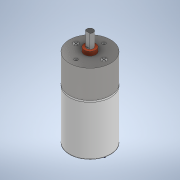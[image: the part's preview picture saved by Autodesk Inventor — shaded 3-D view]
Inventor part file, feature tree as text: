
AUTODESK INVENTOR PART (.ipt)
format: ipt  version: 2022 (Build 260153000, 153)  size: 355,840 bytes
history: native  units: in
note: dims shown in document units (in); Inventor stores cm internally (conversion verified against a paired STEP export)
features: extrude x13, sketch x13, fillet x4, chamfer x1
ambient origin geometry x8: Origin, YZ Plane, XZ Plane, XY Plane, X Axis, Y Axis, Z Axis, Center Point
bodies: Solid1 (feature_tree)
feature tree (31):
  extrude  "Extrusion1"  Depth=1.2205in TaperAngle=0.0deg
  fillet  "Fillet1"  Radius=0.0394in
  extrude  "Extrusion2"  Depth=0.6693in
  extrude  "Extrusion3"  Depth=0.0787in
  extrude  "Extrusion4"  Depth=0.1181in
  extrude  "Extrusion5"  Depth=0.0787in TaperAngle=0.0deg
  fillet  "Fillet2"  Radius=0.1102in
  extrude  "Extrusion6"  Depth=0.0787in TaperAngle=0.0deg
  extrude  "Extrusion7"  Depth=0.0394in
  extrude  "Extrusion8"  Depth=0.0787in
  extrude  "Extrusion9"  Depth=0.0039in
  chamfer  "Chamfer1"  Distance=0.0118in
  extrude  "Extrusion10"  Depth=0.0079in
  extrude  "Extrusion11"  Depth=0.0079in
  extrude  "Extrusion12"  Depth=0.0079in
  fillet  "Fillet3"  Radius=0.0079in
  extrude  "Extrusion13"  Depth=0.7874in
  fillet  "Fillet4"  Radius=0.2756in
  sketch  "Sketch1"  dims[d0=0.9843in d1=1.2205in d2=0.0in d3=0.0394in]
  sketch  "Sketch2"  dims[d4=0.6693in d5=0.0in d6=0.6693in]
  sketch  "Sketch3"  dims[d7=0.0787in d8=0.0787in]
  sketch  "Sketch4"  dims[d9=0.3937in d10=0.0in d11=0.1181in]
  sketch  "Sketch5"  dims[d12=0.1181in d13=0.0787in d14=0.0in d15=0.1102in]
  sketch  "Sketch6"  dims[d16=0.1102in d17=0.0787in d18=0.0in]
  sketch  "Sketch7"  dims[d19=0.0197in d20=0.0394in]
  sketch  "Sketch8"  dims[d21=0.0039in d22=0.0787in]
  sketch  "Sketch9"  dims[d23=0.0079in d24=0.0039in]
  sketch  "Sketch10"  dims[d25=0.0394in]
  sketch  "Sketch11"  dims[d26=0.0079in]
  sketch  "Sketch12"  dims[d27=0.0394in]
  sketch  "Sketch13"  dims[d28=0.0079in d29=0.0118in d30=0.0in d31=0.0079in d32=0.0079in d33=0.0079in d34=0.0079in d35=0.7874in d37=0.6693in d38=0.3937in d40=0.3937in d42=0.2756in d43=0.0984in d44=0.0in d45=0.1575in d46=0.0197in d47=0.0in d48=0.1378in d49=0.315in d50=0.0in d51=0.0039in d52=0.0787in d53=45.0deg d54=0.9803in d55=0.0079in d56=0.0in d57=0.2559in d58=0.0787in d59=0.0in d60=0.7087in d61=0.0039in d62=0.0039in d63=0.0079in d64=0.0118in d65=0.0118in d66=0.1496in d67=0.0in d68=0.0472in d69=0.7874in d71=0.689in d72=0.3937in d74=0.3937in d76=0.047in d77=0.0472in d78=0.0236in d79=0.0in d80=0.0in d81=0.0394in]
